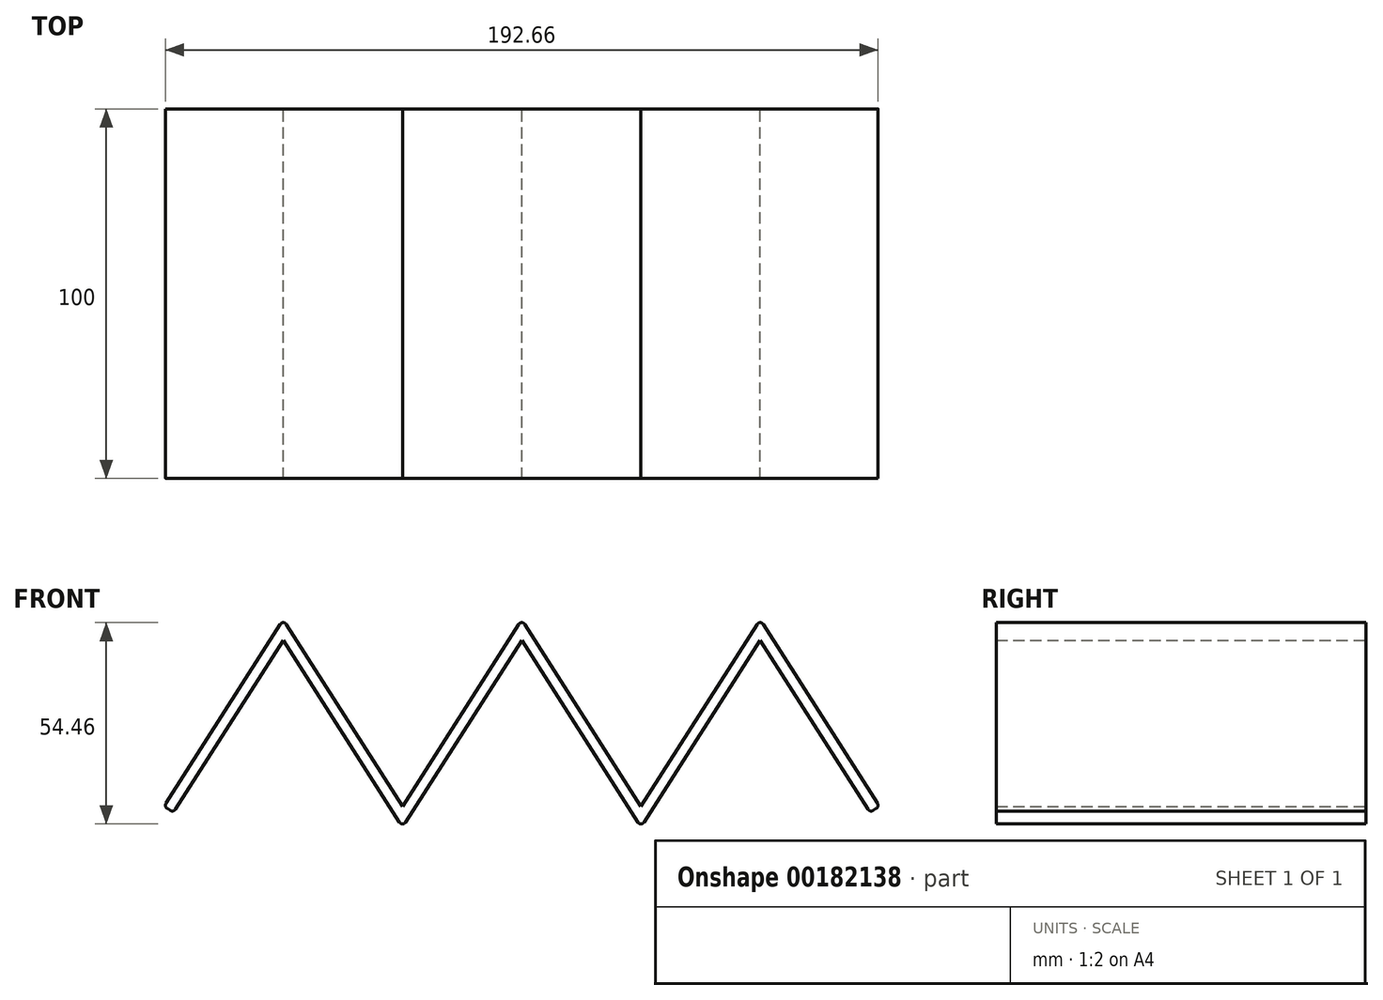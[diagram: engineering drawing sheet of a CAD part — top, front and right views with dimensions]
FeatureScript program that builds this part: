
annotation { "Feature Type Name" : "Feature", "Feature Type Description" : "" }
export const myFeature = defineFeature(function(context is Context, id is Id, definition is map)
    precondition{}
    {
        {
            var Q0;
            Q0=qCreatedBy(makeId("Front.planeOp"),FACE);
            var sketch = newSketch(context, id + "F0", { "sketchPlane" : qUnion([Q0])});
            skLineSegment(sketch, "E0", {"start": v(-107.98, 0) * mm, "end": v(-75.74, 50.6) * mm});
            skLineSegment(sketch, "E1", {"start": v(-75.74, 50.6) * mm, "end": v(-43.5, 0) * mm});
            skLineSegment(sketch, "E2", {"start": v(-75.74, 50.6) * mm, "end": v(-75.74, 0) * mm, "construction": true});
            skLineSegment(sketch, "E3.1.0.0", {"start": v(-43.5, 0) * mm, "end": v(-11.27, 50.6) * mm});
            skLineSegment(sketch, "E3.1.0.1", {"start": v(-11.27, 50.6) * mm, "end": v(20.97, 0) * mm});
            skLineSegment(sketch, "E3.2.0.0", {"start": v(20.97, 0) * mm, "end": v(53.2, 50.6) * mm});
            skLineSegment(sketch, "E3.2.0.1", {"start": v(53.2, 50.6) * mm, "end": v(85.44, 0) * mm});
            skLineSegment(sketch, "E3.direction1", {"start": v(-107.98, 0) * mm, "end": v(-43.5, 0) * mm, "construction": true});
            skLineSegment(sketch, "E4.0", {"start": v(53.2, 45.02) * mm, "end": v(82.91, -1.61) * mm});
            skLineSegment(sketch, "E4.1", {"start": v(20.97, -5.58) * mm, "end": v(53.2, 45.02) * mm});
            skLineSegment(sketch, "E4.2", {"start": v(-105.45, -1.61) * mm, "end": v(-75.74, 45.02) * mm});
            skLineSegment(sketch, "E4.3", {"start": v(-75.74, 45.02) * mm, "end": v(-43.5, -5.58) * mm});
            skLineSegment(sketch, "E4.4", {"start": v(-43.5, -5.58) * mm, "end": v(-11.27, 45.02) * mm});
            skLineSegment(sketch, "E4.5", {"start": v(-11.27, 45.02) * mm, "end": v(20.97, -5.58) * mm});
            skLineSegment(sketch, "E5", {"start": v(-107.98, 0) * mm, "end": v(-105.45, -1.61) * mm});
            skLineSegment(sketch, "E6", {"start": v(82.91, -1.61) * mm, "end": v(85.44, 0) * mm});
            skSolve(sketch);
        }
        {
            var Q0;
            Q0 = qSketchRegion(id + "F0", true);
            extrude(context, id + "F1", {"entities" : qUnion([Q0]), "depth" : 100 * mm});
        }
        {
            var Q0;
            Q0=makeQuery(id+"F1.opExtrude","SWEPT_EDGE",EDGE,{"disambiguationData":[OSD([sQuery(id+"F0.wireOp",EDGE,"E3.2.0.0"),sQuery(id+"F0.wireOp",EDGE,"E3.2.0.1")])]});
            var Q1;
            Q1=makeQuery(id+"F1.opExtrude","SWEPT_EDGE",EDGE,{"disambiguationData":[OSD([sQuery(id+"F0.wireOp",EDGE,"E3.1.0.0"),sQuery(id+"F0.wireOp",EDGE,"E3.1.0.1")])]});
            var Q2;
            Q2=makeQuery(id+"F1.opExtrude","SWEPT_EDGE",EDGE,{"disambiguationData":[OSD([sQuery(id+"F0.wireOp",EDGE,"E0"),sQuery(id+"F0.wireOp",EDGE,"E1")])]});
            var Q3;
            Q3=makeQuery(id+"F1.opExtrude","SWEPT_EDGE",EDGE,{"disambiguationData":[OSD([sQuery(id+"F0.wireOp",EDGE,"E4.3"),sQuery(id+"F0.wireOp",EDGE,"E4.4")])]});
            var Q4;
            Q4=makeQuery(id+"F1.opExtrude","SWEPT_EDGE",EDGE,{"disambiguationData":[OSD([sQuery(id+"F0.wireOp",EDGE,"E4.1"),sQuery(id+"F0.wireOp",EDGE,"E4.5")])]});
            var Q5;
            Q5=makeQuery(id+"F1.opExtrude","SWEPT_EDGE",EDGE,{"disambiguationData":[OSD([sQuery(id+"F0.wireOp",EDGE,"E4.0"),sQuery(id+"F0.wireOp",EDGE,"E6")])]});
            var Q6;
            Q6=makeQuery(id+"F1.opExtrude","SWEPT_EDGE",EDGE,{"disambiguationData":[OSD([sQuery(id+"F0.wireOp",EDGE,"E4.2"),sQuery(id+"F0.wireOp",EDGE,"E5")])]});
            var Q7;
            Q7=makeQuery(id+"F1.opExtrude","SWEPT_EDGE",EDGE,{"disambiguationData":[OSD([sQuery(id+"F0.wireOp",EDGE,"E0"),sQuery(id+"F0.wireOp",EDGE,"E5")])]});
            var Q8;
            Q8=makeQuery(id+"F1.opExtrude","SWEPT_EDGE",EDGE,{"disambiguationData":[OSD([sQuery(id+"F0.wireOp",EDGE,"E3.2.0.1"),sQuery(id+"F0.wireOp",EDGE,"E6")])]});
            fillet(context, id + "F2", {"entities" : qUnion([Q0, Q1, Q2, Q3, Q4, Q5, Q6, Q7, Q8]), "radius" : 1 * mm, "tangentPropagation" : true, "allowEdgeOverflow" : false});
        }
    });
